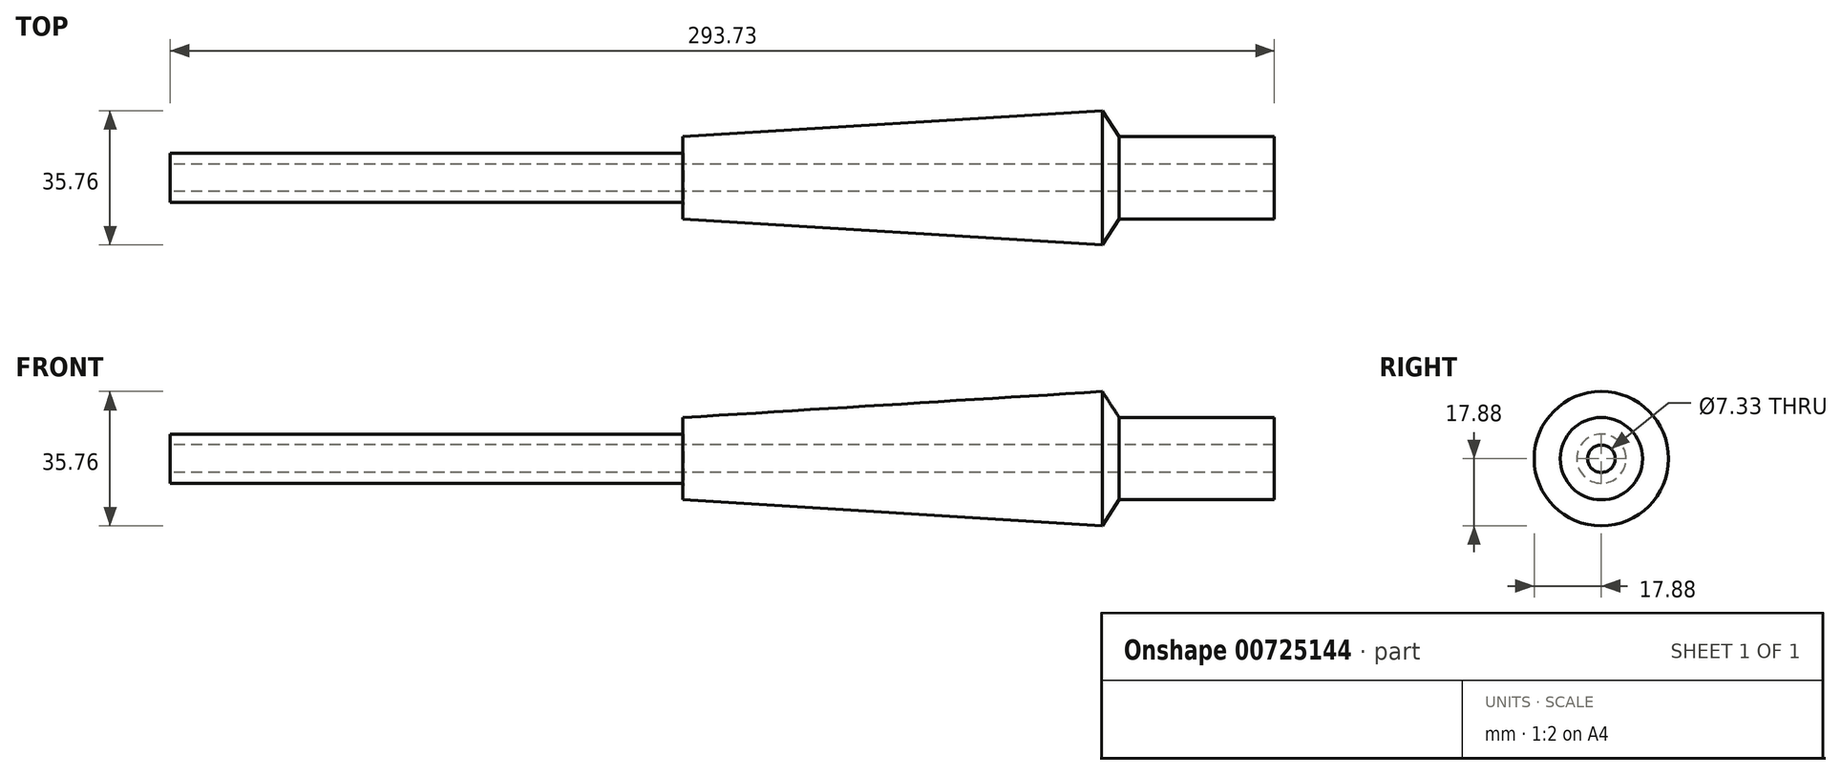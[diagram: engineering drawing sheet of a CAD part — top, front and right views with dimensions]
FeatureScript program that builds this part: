
annotation { "Feature Type Name" : "Feature", "Feature Type Description" : "" }
export const myFeature = defineFeature(function(context is Context, id is Id, definition is map)
    precondition{}
    {
        {
            var Q0;
            Q0=qCreatedBy(makeId("Front.planeOp"),FACE);
            var sketch = newSketch(context, id + "F0", { "sketchPlane" : qUnion([Q0])});
            skLineSegment(sketch, "E0", {"start": v(-128.23, 0) * mm, "end": v(116.95, 0) * mm, "construction": true});
            skLineSegment(sketch, "E1", {"start": v(-122.34, 3.66) * mm, "end": v(116.25, 3.66) * mm});
            skLineSegment(sketch, "E2", {"start": v(116.25, 3.66) * mm, "end": v(116.25, 10.95) * mm});
            skLineSegment(sketch, "E3", {"start": v(116.25, 10.95) * mm, "end": v(74.98, 10.95) * mm});
            skLineSegment(sketch, "E4", {"start": v(74.98, 10.95) * mm, "end": v(70.48, 17.88) * mm});
            skLineSegment(sketch, "E5", {"start": v(70.48, 17.88) * mm, "end": v(-41.2, 10.95) * mm});
            skLineSegment(sketch, "E6", {"start": v(-41.2, 10.95) * mm, "end": v(-40.92, 6.54) * mm});
            skLineSegment(sketch, "E7", {"start": v(-40.92, 6.54) * mm, "end": v(-177.48, 6.54) * mm});
            skLineSegment(sketch, "E8", {"start": v(-177.48, 6.54) * mm, "end": v(-177.48, 3.66) * mm});
            skLineSegment(sketch, "E9", {"start": v(-177.48, 3.66) * mm, "end": v(-122.34, 3.66) * mm});
            skSolve(sketch);
        }
        {
            var Q0;
            Q0=makeQuery(id+"F0.imprint","IMPRINT",FACE,{"disambiguationData":[TD([[makeQuery(id+"F0.imprint","IMPRINT",EDGE,{"derivedFrom":sQuery(id+"F0.wireOp",EDGE,"E1")}),1.0]])]});
            var Q1;
            Q1=sQuery(id+"F0.wireOp",EDGE,"E0");
            revolve(context, id + "F1", {"surfaceOperationType" : NewSurfaceOperationType.NEW, "entities" : qUnion([Q0]), "axis" : qUnion([Q1]), "revolveType" : RevolveType.FULL});
        }
        {
            var Q0;
            Q0=qCreatedBy(makeId("Front.planeOp"),FACE);
            var sketch = newSketch(context, id + "F2", { "sketchPlane" : qUnion([Q0])});
            skLineSegment(sketch, "E10", {"start": v(-176.94, 0) * mm, "end": v(-252.98, 0) * mm});
            skLineSegment(sketch, "E11", {"start": v(-252.98, 0) * mm, "end": v(-315.86, -14.14) * mm});
            skLineSegment(sketch, "E12", {"start": v(-315.86, -14.14) * mm, "end": v(-336.33, -29.73) * mm});
            skCircle(sketch, "E13", {"center": v(-342.17, -34.85) * mm, "radius": 7.76 * mm});
            skPoint(sketch, "E13.second.point", {"position": v(-347.54, -40.46) * mm});
            skPoint(sketch, "E13.third.point", {"position": v(-336.33, -39.97) * mm});
            skSolve(sketch);
        }
    });
